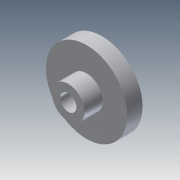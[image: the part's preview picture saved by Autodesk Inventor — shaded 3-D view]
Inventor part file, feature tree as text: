
AUTODESK INVENTOR PART (.ipt)
format: ipt  version: 2015 (Build 190159000, 159)  size: 124,928 bytes
history: native  units: mm
features: sketch x8, extrude x7
ambient origin geometry x8: Origin, YZ Plane, XZ Plane, XY Plane, X Axis, Y Axis, Z Axis, Center Point
bodies: Solid1 (feature_tree)
feature tree (15):
  sketch  "Sketch1"  dims[d0=20.0mm d1=1.8mm d2=0.0mm]
  sketch  "Sketch2"  dims[d3=7.0mm d4=5.0mm]
  extrude  "Extrusion1"  Depth=1.8mm TaperAngle=0.0deg
  extrude  "Extrusion2"  Depth=5.0mm
  extrude  "Extrusion3"  Depth=2.4mm
  extrude  "Extrusion4"  Depth=2.4mm TaperAngle=0.0deg
  extrude  "Extrusion5"  Depth=3.0mm
  extrude  "Extrusion6"  Depth=1.8mm TaperAngle=0.0deg
  extrude  "Extrusion7"  Depth=2.0mm
  sketch  "Sketch3"  dims[d5=2.4mm d6=0.0mm d7=6.3mm]
  sketch  "Sketch4"  dims[d8=3.0mm d9=2.4mm d10=0.0mm]
  sketch  "Sketch5"  dims[d11=6.3mm d12=3.0mm]
  sketch  "Sketch6"  dims[d13=2.0mm d14=0.0mm d15=1.8mm d16=0.0mm]
  sketch  "Sketch7"  dims[d17=2.0mm d18=0.0mm d19=8.0mm]
  sketch  "Sketch8"  dims[d20=4.0mm d21=4.5mm d22=0.0mm]
